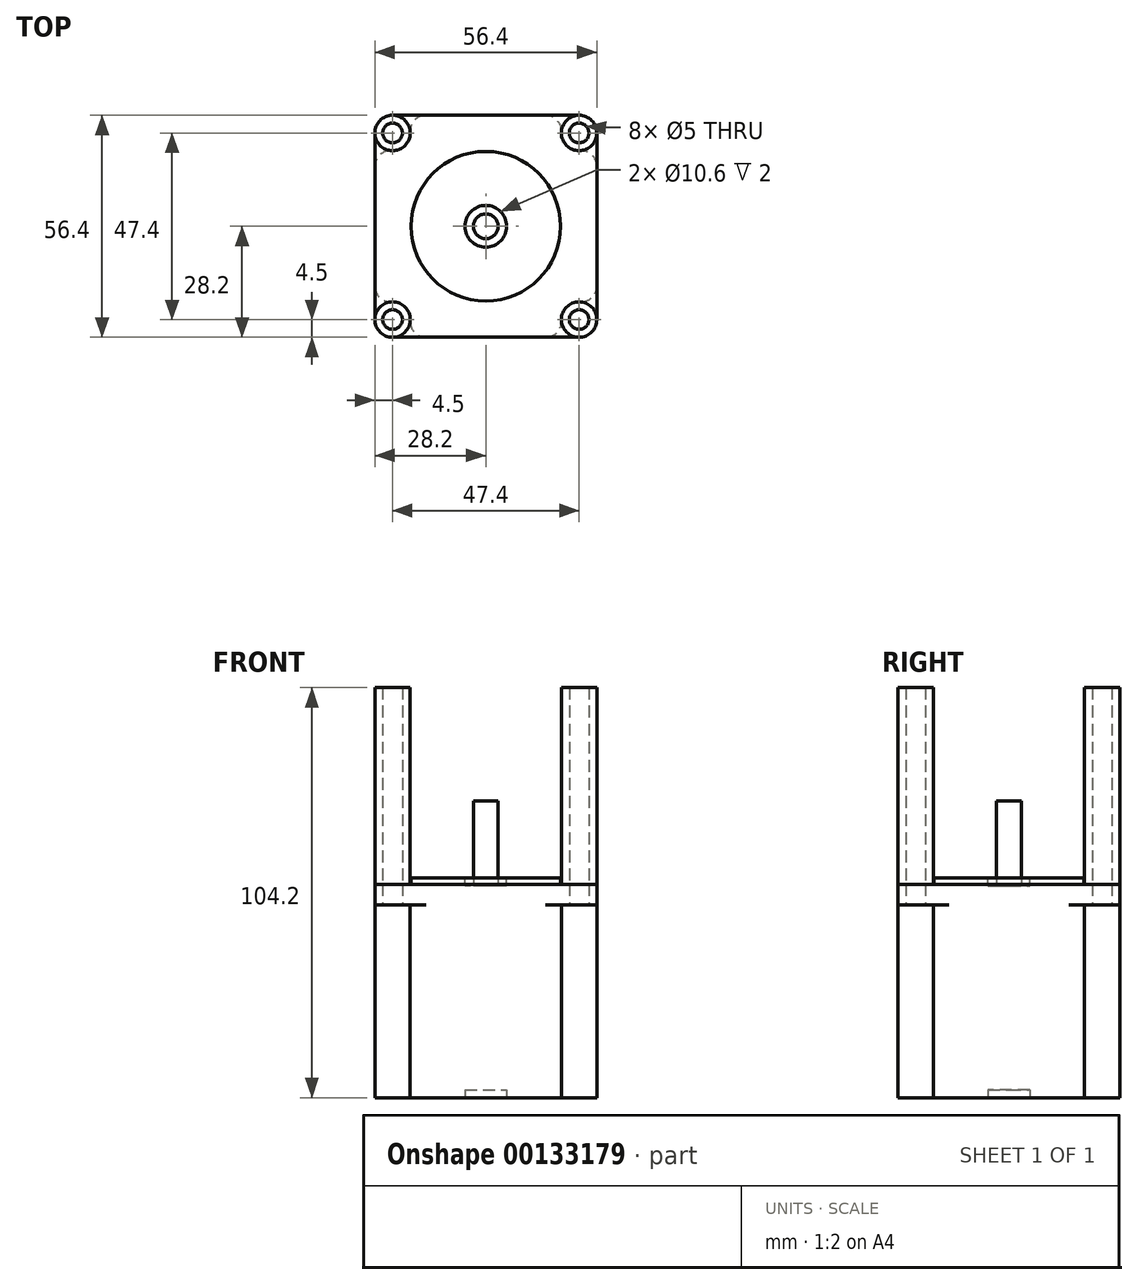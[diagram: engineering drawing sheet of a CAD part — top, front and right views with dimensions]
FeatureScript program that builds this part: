
annotation { "Feature Type Name" : "Feature", "Feature Type Description" : "" }
export const myFeature = defineFeature(function(context is Context, id is Id, definition is map)
    precondition{}
    {
        {
            var Q0;
            Q0=qCreatedBy(makeId("Top.planeOp"),FACE);
            var sketch = newSketch(context, id + "F0", { "sketchPlane" : qUnion([Q0])});
            skLineSegment(sketch, "E0.bottom", {"start": v(-23.7, 28.2) * mm, "end": v(23.7, 28.2) * mm});
            skLineSegment(sketch, "E0.top", {"start": v(-23.7, -28.2) * mm, "end": v(23.7, -28.2) * mm});
            skLineSegment(sketch, "E0.left", {"start": v(-28.2, 23.7) * mm, "end": v(-28.2, -23.7) * mm});
            skLineSegment(sketch, "E0.right", {"start": v(28.2, 23.7) * mm, "end": v(28.2, -23.7) * mm});
            skPoint(sketch, "E1.visualSharp", {"position": v(-28.2, 28.2) * mm});
            skArc(sketch, "E1.filletArc", {"start": v(-23.7, 28.2) * mm, "mid": v(-26.88, 26.88) * mm, "end": v(-28.2, 23.7) * mm});
            skPoint(sketch, "E2.visualSharp", {"position": v(28.2, 28.2) * mm});
            skArc(sketch, "E2.filletArc", {"start": v(28.2, 23.7) * mm, "mid": v(26.88, 26.88) * mm, "end": v(23.7, 28.2) * mm});
            skPoint(sketch, "E3.visualSharp", {"position": v(28.2, -28.2) * mm});
            skArc(sketch, "E3.filletArc", {"start": v(23.7, -28.2) * mm, "mid": v(26.88, -26.88) * mm, "end": v(28.2, -23.7) * mm});
            skPoint(sketch, "E4.visualSharp", {"position": v(-28.2, -28.2) * mm});
            skArc(sketch, "E4.filletArc", {"start": v(-28.2, -23.7) * mm, "mid": v(-26.88, -26.88) * mm, "end": v(-23.7, -28.2) * mm});
            skCircle(sketch, "E5", {"center": v(-23.7, -23.7) * mm, "radius": 2.5 * mm});
            skCircle(sketch, "E6", {"center": v(23.7, -23.7) * mm, "radius": 2.5 * mm});
            skCircle(sketch, "E7", {"center": v(-23.7, 23.7) * mm, "radius": 2.5 * mm});
            skCircle(sketch, "E8", {"center": v(23.7, 23.7) * mm, "radius": 2.5 * mm});
            skSolve(sketch);
        }
        {
            var Q0;
            Q0=makeQuery(id+"F0.imprint","IMPRINT",FACE,{"disambiguationData":[TD([[makeQuery(id+"F0.imprint","IMPRINT",EDGE,{"derivedFrom":sQuery(id+"F0.wireOp",EDGE,"E0.bottom")}),-1.0]])]});
            extrude(context, id + "F1", {"entities" : qUnion([Q0]), "depth" : 5.2 * mm});
        }
        {
            var Q0;
            Q0=makeQuery(id+"F1.opExtrude","CAP_FACE",FACE,{"disambiguationData":[OSD([sQuery(id+"F0.wireOp",EDGE,"E0.bottom"),sQuery(id+"F0.wireOp",EDGE,"E0.top"),sQuery(id+"F0.wireOp",EDGE,"E0.left"),sQuery(id+"F0.wireOp",EDGE,"E0.right"),sQuery(id+"F0.wireOp",EDGE,"E1.filletArc"),sQuery(id+"F0.wireOp",EDGE,"E2.filletArc"),sQuery(id+"F0.wireOp",EDGE,"E3.filletArc"),sQuery(id+"F0.wireOp",EDGE,"E4.filletArc"),sQuery(id+"F0.wireOp",EDGE,"E5"),sQuery(id+"F0.wireOp",EDGE,"E6"),sQuery(id+"F0.wireOp",EDGE,"E7"),sQuery(id+"F0.wireOp",EDGE,"E8")])],"isStart":true});
            var sketch = newSketch(context, id + "F2", { "sketchPlane" : qUnion([Q0])});
            skLineSegment(sketch, "E9.bottom", {"start": v(-15.21, -28.2) * mm, "end": v(15.21, -28.2) * mm});
            skLineSegment(sketch, "E9.top", {"start": v(-15.21, 28.2) * mm, "end": v(15.21, 28.2) * mm});
            skLineSegment(sketch, "E9.left", {"start": v(-28.2, -15.21) * mm, "end": v(-28.2, 15.21) * mm});
            skLineSegment(sketch, "E9.right", {"start": v(28.2, -15.21) * mm, "end": v(28.2, 15.21) * mm});
            skArc(sketch, "E10", {"start": v(-23.96, 19.2) * mm, "mid": v(-20.52, 20.52) * mm, "end": v(-19.2, 23.96) * mm});
            skArc(sketch, "E11", {"start": v(19.2, 23.96) * mm, "mid": v(20.52, 20.52) * mm, "end": v(23.96, 19.2) * mm});
            skArc(sketch, "E12", {"start": v(23.96, -19.2) * mm, "mid": v(20.52, -20.52) * mm, "end": v(19.2, -23.96) * mm});
            skArc(sketch, "E13", {"start": v(-19.2, -23.96) * mm, "mid": v(-20.52, -20.52) * mm, "end": v(-23.96, -19.2) * mm});
            skPoint(sketch, "E14.orphan", {"position": v(-28.2, -28.2) * mm});
            skPoint(sketch, "E15.orphan", {"position": v(28.2, 28.2) * mm});
            skPoint(sketch, "E16.visualSharp", {"position": v(-28.2, -23.7) * mm});
            skArc(sketch, "E16.filletArc", {"start": v(-28.2, -15.21) * mm, "mid": v(-26.94, -18.13) * mm, "end": v(-23.96, -19.2) * mm});
            skPoint(sketch, "E17.visualSharp", {"position": v(-23.7, -28.2) * mm});
            skArc(sketch, "E17.filletArc", {"start": v(-19.2, -23.96) * mm, "mid": v(-18.13, -26.94) * mm, "end": v(-15.21, -28.2) * mm});
            skPoint(sketch, "E18.visualSharp", {"position": v(23.7, -28.2) * mm});
            skArc(sketch, "E18.filletArc", {"start": v(15.21, -28.2) * mm, "mid": v(18.13, -26.94) * mm, "end": v(19.2, -23.96) * mm});
            skPoint(sketch, "E19.visualSharp", {"position": v(28.2, -23.7) * mm});
            skArc(sketch, "E19.filletArc", {"start": v(23.96, -19.2) * mm, "mid": v(26.94, -18.13) * mm, "end": v(28.2, -15.21) * mm});
            skPoint(sketch, "E20.visualSharp", {"position": v(28.2, 23.7) * mm});
            skArc(sketch, "E20.filletArc", {"start": v(28.2, 15.21) * mm, "mid": v(26.94, 18.13) * mm, "end": v(23.96, 19.2) * mm});
            skPoint(sketch, "E21.visualSharp", {"position": v(23.7, 28.2) * mm});
            skArc(sketch, "E21.filletArc", {"start": v(19.2, 23.96) * mm, "mid": v(18.13, 26.94) * mm, "end": v(15.21, 28.2) * mm});
            skPoint(sketch, "E22.visualSharp", {"position": v(-23.7, 28.2) * mm});
            skArc(sketch, "E22.filletArc", {"start": v(-15.21, 28.2) * mm, "mid": v(-18.13, 26.94) * mm, "end": v(-19.2, 23.96) * mm});
            skPoint(sketch, "E23.visualSharp", {"position": v(-28.2, 23.7) * mm});
            skArc(sketch, "E23.filletArc", {"start": v(-23.96, 19.2) * mm, "mid": v(-26.94, 18.13) * mm, "end": v(-28.2, 15.21) * mm});
            skSolve(sketch);
        }
        {
            var Q0;
            Q0=makeQuery(id+"F2.imprint","IMPRINT",FACE,{"disambiguationData":[TD([[makeQuery(id+"F2.imprint","IMPRINT",EDGE,{"derivedFrom":sQuery(id+"F2.wireOp",EDGE,"E9.bottom")}),1.0]])]});
            extrude(context, id + "F3", {"entities" : qUnion([Q0]), "operationType" : NewBodyOperationType.ADD, "depth" : 49 * mm});
        }
        {
            var Q0;
            Q0=makeQuery(id+"F1.opExtrude","CAP_FACE",FACE,{"disambiguationData":[OSD([sQuery(id+"F0.wireOp",EDGE,"E0.bottom"),sQuery(id+"F0.wireOp",EDGE,"E0.top"),sQuery(id+"F0.wireOp",EDGE,"E0.left"),sQuery(id+"F0.wireOp",EDGE,"E0.right"),sQuery(id+"F0.wireOp",EDGE,"E1.filletArc"),sQuery(id+"F0.wireOp",EDGE,"E2.filletArc"),sQuery(id+"F0.wireOp",EDGE,"E3.filletArc"),sQuery(id+"F0.wireOp",EDGE,"E4.filletArc"),sQuery(id+"F0.wireOp",EDGE,"E5"),sQuery(id+"F0.wireOp",EDGE,"E6"),sQuery(id+"F0.wireOp",EDGE,"E7"),sQuery(id+"F0.wireOp",EDGE,"E8")])],"isStart":false});
            var sketch = newSketch(context, id + "F4", { "sketchPlane" : qUnion([Q0])});
            skCircle(sketch, "E24", {"center": v(0, 0) * mm, "radius": 19 * mm});
            skSolve(sketch);
        }
        {
            var Q0;
            Q0=makeQuery(id+"F4.imprint","IMPRINT",FACE,{"disambiguationData":[TD([[makeQuery(id+"F4.imprint","IMPRINT",EDGE,{"derivedFrom":sQuery(id+"F4.wireOp",EDGE,"E24")}),1.0]])]});
            extrude(context, id + "F5", {"entities" : qUnion([Q0]), "operationType" : NewBodyOperationType.ADD, "depth" : 1.6 * mm});
        }
        {
            var Q0;
            Q0=makeQuery(id+"F5.opExtrude","CAP_FACE",FACE,{"disambiguationData":[OSD([sQuery(id+"F4.wireOp",EDGE,"E24")])],"isStart":false});
            var sketch = newSketch(context, id + "F6", { "sketchPlane" : qUnion([Q0])});
            skCircle(sketch, "E25", {"center": v(0, 0) * mm, "radius": 5.3 * mm});
            skSolve(sketch);
        }
        {
            var Q0;
            Q0=makeQuery(id+"F3.opExtrude","CAP_FACE",FACE,{"disambiguationData":[OSD([sQuery(id+"F2.wireOp",EDGE,"E9.bottom"),sQuery(id+"F2.wireOp",EDGE,"E9.top"),sQuery(id+"F2.wireOp",EDGE,"E9.left"),sQuery(id+"F2.wireOp",EDGE,"E9.right"),sQuery(id+"F2.wireOp",EDGE,"E10"),sQuery(id+"F2.wireOp",EDGE,"E11"),sQuery(id+"F2.wireOp",EDGE,"E12"),sQuery(id+"F2.wireOp",EDGE,"E13"),sQuery(id+"F2.wireOp",EDGE,"E16.filletArc"),sQuery(id+"F2.wireOp",EDGE,"E17.filletArc"),sQuery(id+"F2.wireOp",EDGE,"E18.filletArc"),sQuery(id+"F2.wireOp",EDGE,"E19.filletArc"),sQuery(id+"F2.wireOp",EDGE,"E20.filletArc"),sQuery(id+"F2.wireOp",EDGE,"E21.filletArc"),sQuery(id+"F2.wireOp",EDGE,"E22.filletArc"),sQuery(id+"F2.wireOp",EDGE,"E23.filletArc")])],"isStart":false});
            var sketch = newSketch(context, id + "F7", { "sketchPlane" : qUnion([Q0])});
            skCircle(sketch, "E26", {"center": v(0, 0) * mm, "radius": 5.3 * mm});
            skSolve(sketch);
        }
        {
            var Q0;
            Q0=makeQuery(id+"F6.imprint","IMPRINT",FACE,{"disambiguationData":[TD([[makeQuery(id+"F6.imprint","IMPRINT",EDGE,{"derivedFrom":sQuery(id+"F6.wireOp",EDGE,"E25")}),1.0]])]});
            extrude(context, id + "F8", {"entities" : qUnion([Q0]), "operationType" : NewBodyOperationType.REMOVE, "oppositeDirection" : true, "depth" : 2 * mm});
        }
        {
            var Q0;
            Q0=makeQuery(id+"F8.boolean.opBoolean","COPY",FACE,{"derivedFrom":makeQuery(id+"F8.opExtrude","CAP_FACE",FACE,{"disambiguationData":[OSD([sQuery(id+"F6.wireOp",EDGE,"E25")])],"isStart":false})});
            var sketch = newSketch(context, id + "F9", { "sketchPlane" : qUnion([Q0])});
            skCircle(sketch, "E27", {"center": v(0, 0) * mm, "radius": 3.15 * mm});
            skSolve(sketch);
        }
        {
            var Q0;
            Q0=makeQuery(id+"F9.imprint","IMPRINT",FACE,{"disambiguationData":[TD([[makeQuery(id+"F9.imprint","IMPRINT",EDGE,{"derivedFrom":sQuery(id+"F9.wireOp",EDGE,"E27")}),1.0]])]});
            extrude(context, id + "F10", {"entities" : qUnion([Q0]), "depth" : 21.6 * mm});
        }
        {
            var Q0;
            Q0 = qSketchRegion(id + "F7", true);
            extrude(context, id + "F11", {"entities" : qUnion([Q0]), "operationType" : NewBodyOperationType.REMOVE, "oppositeDirection" : true, "depth" : 2 * mm});
        }
        {
            var Q0;
            Q0=makeQuery(id+"F1.opExtrude","CAP_FACE",FACE,{"disambiguationData":[OSD([sQuery(id+"F0.wireOp",EDGE,"E0.bottom"),sQuery(id+"F0.wireOp",EDGE,"E0.top"),sQuery(id+"F0.wireOp",EDGE,"E0.left"),sQuery(id+"F0.wireOp",EDGE,"E0.right"),sQuery(id+"F0.wireOp",EDGE,"E1.filletArc"),sQuery(id+"F0.wireOp",EDGE,"E2.filletArc"),sQuery(id+"F0.wireOp",EDGE,"E3.filletArc"),sQuery(id+"F0.wireOp",EDGE,"E4.filletArc"),sQuery(id+"F0.wireOp",EDGE,"E5"),sQuery(id+"F0.wireOp",EDGE,"E6"),sQuery(id+"F0.wireOp",EDGE,"E7"),sQuery(id+"F0.wireOp",EDGE,"E8")])],"isStart":false});
            var sketch = newSketch(context, id + "F12", { "sketchPlane" : qUnion([Q0])});
            skCircle(sketch, "E28", {"center": v(23.7, 23.7) * mm, "radius": 2.5 * mm});
            skCircle(sketch, "E29", {"center": v(-23.7, 23.7) * mm, "radius": 2.5 * mm});
            skCircle(sketch, "E30", {"center": v(-23.7, -23.7) * mm, "radius": 2.5 * mm});
            skCircle(sketch, "E31", {"center": v(23.7, -23.7) * mm, "radius": 2.5 * mm});
            skCircle(sketch, "E32", {"center": v(-23.7, 23.7) * mm, "radius": 4.5 * mm});
            skCircle(sketch, "E33", {"center": v(23.7, 23.7) * mm, "radius": 4.5 * mm});
            skCircle(sketch, "E34", {"center": v(23.7, -23.7) * mm, "radius": 4.5 * mm});
            skCircle(sketch, "E35", {"center": v(-23.7, -23.7) * mm, "radius": 4.5 * mm});
            skSolve(sketch);
        }
        {
            var Q0;
            Q0=makeQuery(id+"F12.imprint","IMPRINT",FACE,{"disambiguationData":[TD([[makeQuery(id+"F12.imprint","IMPRINT",EDGE,{"derivedFrom":sQuery(id+"F12.wireOp",EDGE,"E31")}),-1.0]])]});
            var Q1;
            Q1=makeQuery(id+"F12.imprint","IMPRINT",FACE,{"disambiguationData":[TD([[makeQuery(id+"F12.imprint","IMPRINT",EDGE,{"derivedFrom":sQuery(id+"F12.wireOp",EDGE,"E30")}),-1.0]])]});
            var Q2;
            Q2=makeQuery(id+"F12.imprint","IMPRINT",FACE,{"disambiguationData":[TD([[makeQuery(id+"F12.imprint","IMPRINT",EDGE,{"derivedFrom":sQuery(id+"F12.wireOp",EDGE,"E29")}),-1.0]])]});
            var Q3;
            Q3=makeQuery(id+"F12.imprint","IMPRINT",FACE,{"disambiguationData":[TD([[makeQuery(id+"F12.imprint","IMPRINT",EDGE,{"derivedFrom":sQuery(id+"F12.wireOp",EDGE,"E28")}),-1.0]])]});
            extrude(context, id + "F13", {"entities" : qUnion([Q0, Q1, Q2, Q3]), "depth" : 50 * mm});
        }
    });
